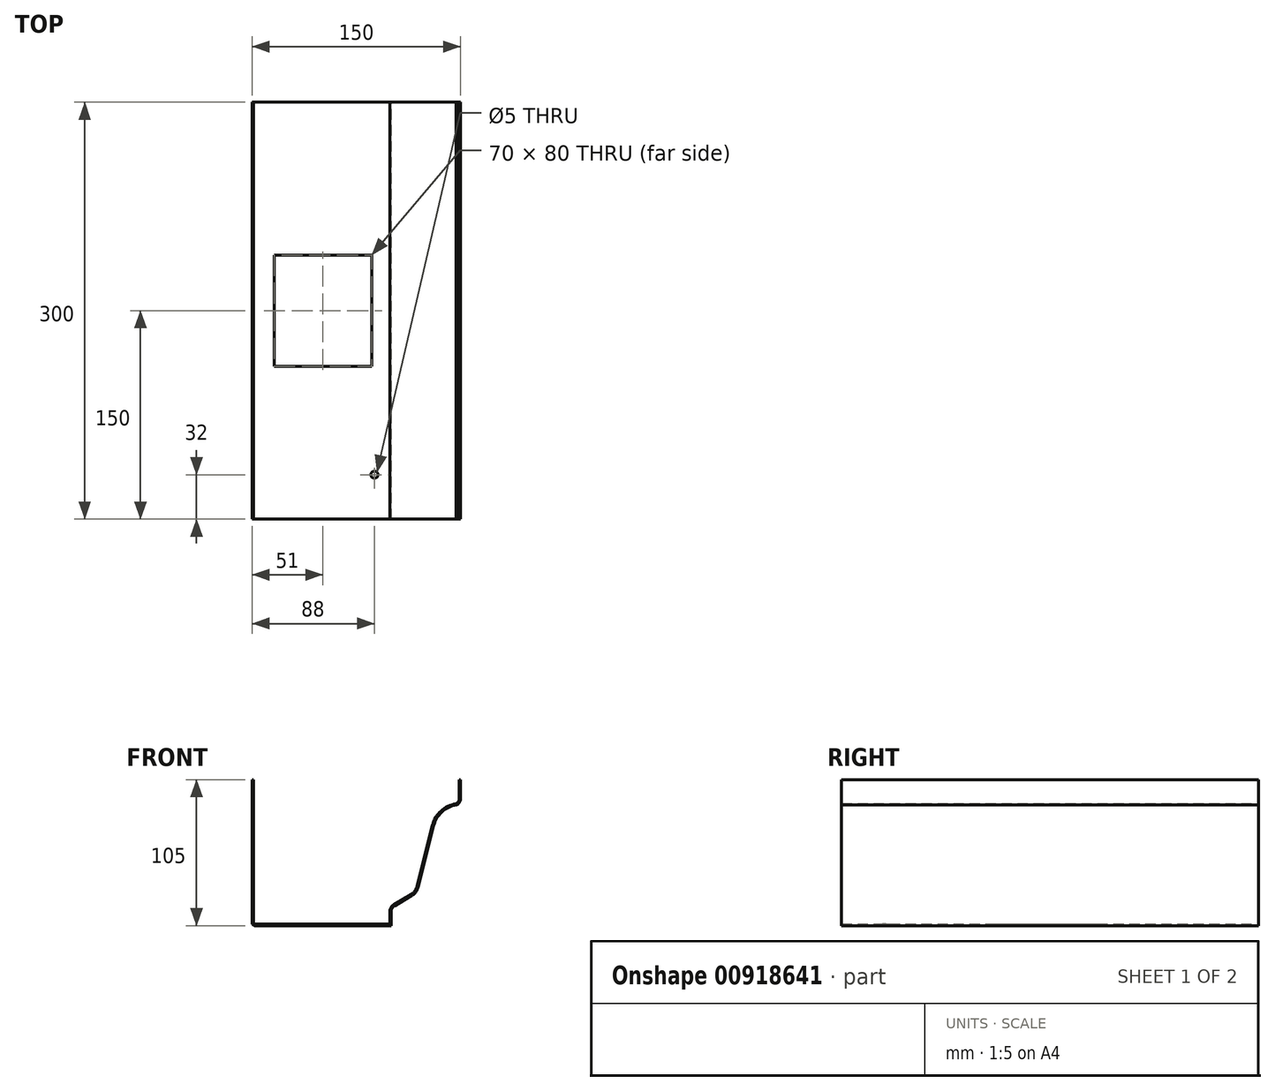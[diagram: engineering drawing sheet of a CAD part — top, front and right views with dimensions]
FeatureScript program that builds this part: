
annotation { "Feature Type Name" : "Feature", "Feature Type Description" : "" }
export const myFeature = defineFeature(function(context is Context, id is Id, definition is map)
    precondition{}
    {
        {
            var Q0;
            Q0=qCreatedBy(makeId("Front.planeOp"),FACE);
            var sketch = newSketch(context, id + "F0", { "sketchPlane" : qUnion([Q0])});
            skLineSegment(sketch, "E0.right", {"start": v(75, 52.5) * mm, "end": v(75, 38.91) * mm});
            skPoint(sketch, "E0.middle", {"position": v(0, 0) * mm});
            skArc(sketch, "E1", {"start": v(71.93, 34.26) * mm, "mid": v(61.54, 29.3) * mm, "end": v(55.61, 19.41) * mm});
            skArc(sketch, "E2", {"start": v(39.92, -30.84) * mm, "mid": v(42.75, -28.3) * mm, "end": v(44.39, -24.88) * mm});
            skArc(sketch, "E3", {"start": v(27.46, -38.2) * mm, "mid": v(25.66, -40.02) * mm, "end": v(25, -42.5) * mm});
            skLineSegment(sketch, "E4", {"start": v(27.46, -38.2) * mm, "end": v(39.92, -30.84) * mm});
            skLineSegment(sketch, "E5", {"start": v(44.39, -24.88) * mm, "end": v(55.61, 19.41) * mm});
            skArc(sketch, "E6", {"start": v(71.93, 34.26) * mm, "mid": v(74.17, 36.12) * mm, "end": v(75, 38.91) * mm});
            skPoint(sketch, "E7.orphan", {"position": v(-75, -52.5) * mm});
            skPoint(sketch, "E0.left.start.orphan", {"position": v(-75, 52.5) * mm});
            skPoint(sketch, "E8.right.start.orphan", {"position": v(25, -52.5) * mm});
            skLineSegment(sketch, "E9", {"start": v(-73, -52.5) * mm, "end": v(25, -52.5) * mm});
            skLineSegment(sketch, "E10", {"start": v(25, -52.5) * mm, "end": v(25, -42.5) * mm});
            skLineSegment(sketch, "E11", {"start": v(-75, -50.5) * mm, "end": v(-75, 52.5) * mm});
            skLineSegment(sketch, "E12", {"start": v(-74, 52.5) * mm, "end": v(-75, 52.5) * mm});
            skLineSegment(sketch, "E13", {"start": v(-74, 52.5) * mm, "end": v(-74, -50.5) * mm});
            skLineSegment(sketch, "E14", {"start": v(-73, -51.5) * mm, "end": v(24, -51.5) * mm});
            skLineSegment(sketch, "E15", {"start": v(24, -51.5) * mm, "end": v(24, -42.5) * mm});
            skLineSegment(sketch, "E16", {"start": v(26.95, -37.33) * mm, "end": v(39.41, -29.98) * mm});
            skLineSegment(sketch, "E17", {"start": v(74, 52.5) * mm, "end": v(74, 38.88) * mm});
            skLineSegment(sketch, "E18", {"start": v(74, 52.5) * mm, "end": v(75, 52.5) * mm});
            skArc(sketch, "E19.trimOffspring", {"start": v(26.95, -37.33) * mm, "mid": v(24.79, -39.52) * mm, "end": v(24, -42.5) * mm});
            skArc(sketch, "E20", {"start": v(39.41, -29.98) * mm, "mid": v(41.95, -27.7) * mm, "end": v(43.42, -24.63) * mm});
            skArc(sketch, "E21", {"start": v(71.65, 35.23) * mm, "mid": v(60.82, 29.99) * mm, "end": v(54.64, 19.66) * mm});
            skLineSegment(sketch, "E22", {"start": v(54.64, 19.66) * mm, "end": v(43.42, -24.63) * mm});
            skArc(sketch, "E23", {"start": v(71.65, 35.23) * mm, "mid": v(73.36, 36.7) * mm, "end": v(74, 38.88) * mm});
            skPoint(sketch, "E24", {"position": v(-73, -50.5) * mm});
            skArc(sketch, "E25", {"start": v(-74, -50.5) * mm, "mid": v(-73.7, -51.2) * mm, "end": v(-73, -51.5) * mm});
            skArc(sketch, "E26", {"start": v(-75, -50.5) * mm, "mid": v(-74.41, -51.91) * mm, "end": v(-73, -52.5) * mm});
            skPoint(sketch, "E27.orphan", {"position": v(-74, -51.5) * mm});
            skSolve(sketch);
        }
        {
            var Q0;
            Q0=qSketchRegion(id+"F0",true);
            extrude(context, id + "F1", {"entities" : qUnion([Q0]), "depth" : 300 * mm, "offsetDistance" : 25 * mm});
        }
        {
            var Q0;
            Q0=makeQuery(id+"F1.opExtrude","SWEPT_FACE",FACE,{"disambiguationData":[OSD([sQuery(id+"F0.wireOp",EDGE,"E9")])]});
            var sketch = newSketch(context, id + "F2", { "sketchPlane" : qUnion([Q0])});
            skPoint(sketch, "E28", {"position": v(-24, 150) * mm});
            skPoint(sketch, "E28.positionSnap0", {"position": v(-24, 0) * mm});
            skPoint(sketch, "E28.positionSnap1", {"position": v(25, 150) * mm});
            skLineSegment(sketch, "E29.bottom", {"start": v(11, 110) * mm, "end": v(-59, 110) * mm});
            skLineSegment(sketch, "E29.top", {"start": v(11, 190) * mm, "end": v(-59, 190) * mm});
            skLineSegment(sketch, "E29.left", {"start": v(11, 110) * mm, "end": v(11, 190) * mm});
            skLineSegment(sketch, "E29.right", {"start": v(-59, 110) * mm, "end": v(-59, 190) * mm});
            skSolve(sketch);
        }
        {
            var Q0;
            Q0=qSketchRegion(id+"F2",true);
            extrude(context, id + "F3", {"entities" : qUnion([Q0]), "operationType" : NewBodyOperationType.REMOVE, "oppositeDirection" : true, "depth" : 25 * mm, "offsetDistance" : 25 * mm});
        }
        {
            var Q0;
            Q0=qSketchRegion(id+"F2",true);
            extrude(context, id + "F4", {"entities" : qUnion([Q0]), "operationType" : NewBodyOperationType.REMOVE, "oppositeDirection" : true, "depth" : 25 * mm, "offsetDistance" : 25 * mm});
        }
        {
            var Q0;
            Q0=qSketchRegion(id+"F2",true);
            extrude(context, id + "F5", {"entities" : qUnion([Q0]), "operationType" : NewBodyOperationType.REMOVE, "oppositeDirection" : true, "depth" : 25 * mm, "offsetDistance" : 25 * mm});
        }
        {
            var Q0;
            Q0=makeQuery(id+"F1.opExtrude","SWEPT_FACE",FACE,{"disambiguationData":[OSD([sQuery(id+"F0.wireOp",EDGE,"E9")])]});
            var sketch = newSketch(context, id + "F6", { "sketchPlane" : qUnion([Q0])});
            skPoint(sketch, "E30", {"position": v(13, 268) * mm});
            skCircle(sketch, "E31", {"center": v(13, 268) * mm, "radius": 2.5 * mm});
            skSolve(sketch);
        }
        {
            var Q0;
            Q0 = qSketchRegion(id + "F6", true);
            extrude(context, id + "F7", {"entities" : qUnion([Q0]), "operationType" : NewBodyOperationType.REMOVE, "oppositeDirection" : true, "depth" : 25 * mm, "offsetDistance" : 25 * mm});
        }
    });
